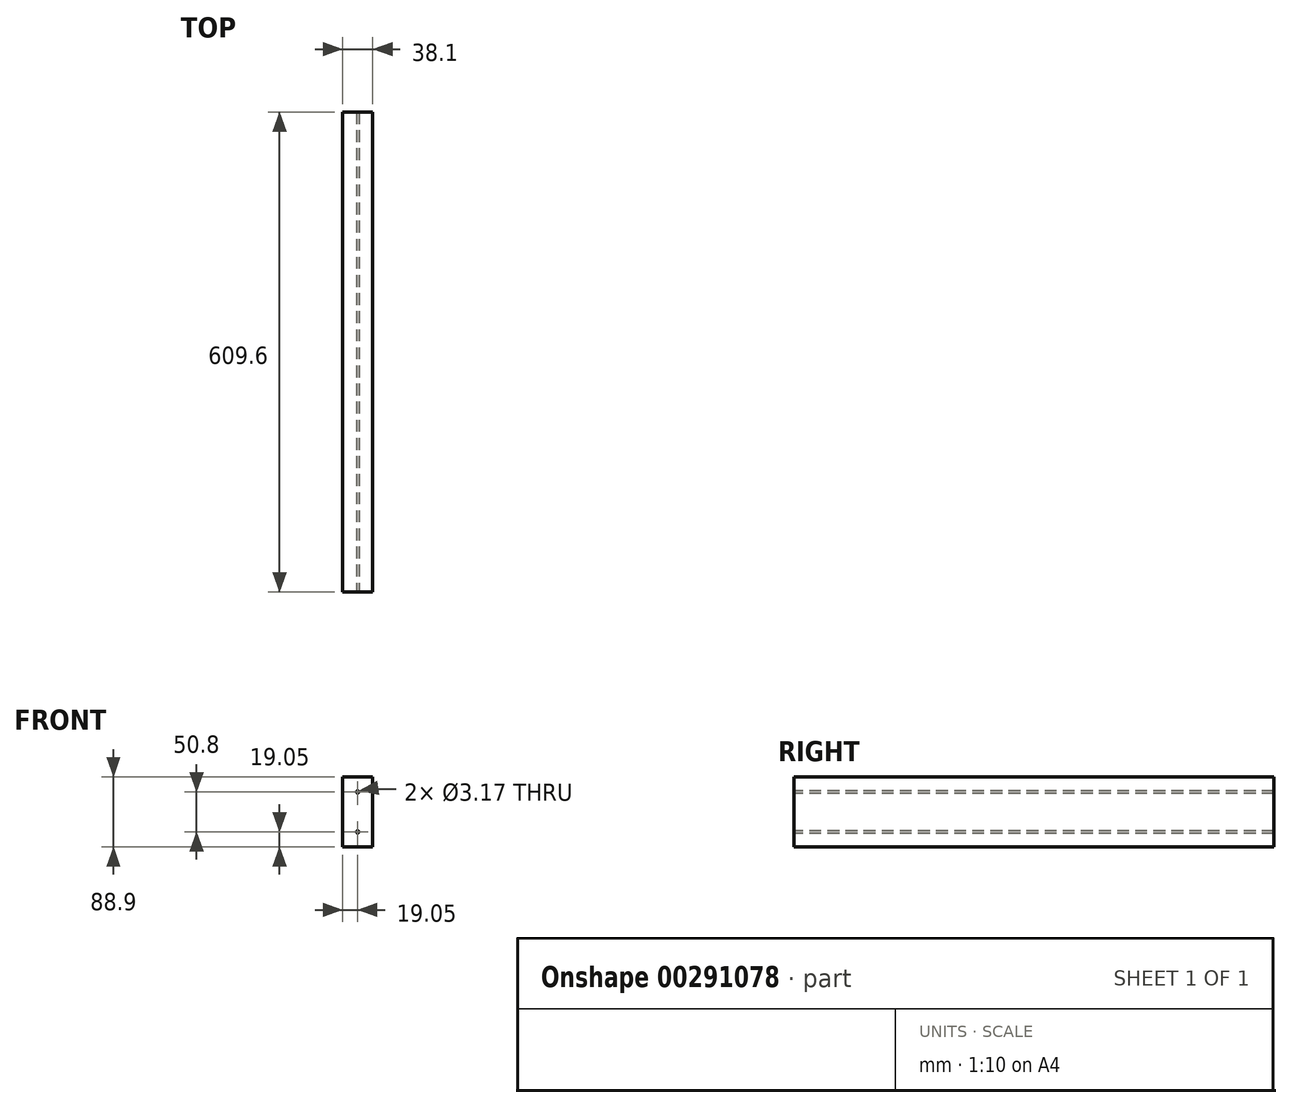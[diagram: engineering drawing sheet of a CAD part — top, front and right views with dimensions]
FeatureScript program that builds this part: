
annotation { "Feature Type Name" : "Feature", "Feature Type Description" : "" }
export const myFeature = defineFeature(function(context is Context, id is Id, definition is map)
    precondition{}
    {
        {
            var Q0;
            Q0=qCreatedBy(makeId("Right.planeOp"),FACE);
            var sketch = newSketch(context, id + "F0", { "sketchPlane" : qUnion([Q0])});
            skLineSegment(sketch, "E0.bottom", {"start": v(0, 0) * mm, "end": v(609.6, 0) * mm});
            skLineSegment(sketch, "E0.top", {"start": v(0, -88.9) * mm, "end": v(609.6, -88.9) * mm});
            skLineSegment(sketch, "E0.left", {"start": v(0, 0) * mm, "end": v(0, -88.9) * mm});
            skLineSegment(sketch, "E0.right", {"start": v(609.6, 0) * mm, "end": v(609.6, -88.9) * mm});
            skSolve(sketch);
        }
        {
            var Q0;
            Q0 = qSketchRegion(id + "F0", true);
            extrude(context, id + "F1", {"entities" : qUnion([Q0]), "oppositeDirection" : true, "depth" : 38.1 * mm});
        }
        {
            var Q0;
            Q0=qCreatedBy(makeId("Front.planeOp"),FACE);
            var sketch = newSketch(context, id + "F2", { "sketchPlane" : qUnion([Q0])});
            skCircle(sketch, "E1", {"center": v(-19.05, -19.05) * mm, "radius": 1.59 * mm});
            skCircle(sketch, "E2.0.1.0", {"center": v(-19.05, -69.85) * mm, "radius": 1.59 * mm});
            skLineSegment(sketch, "E2.direction1", {"start": v(-19.05, -19.05) * mm, "end": v(6.35, -19.05) * mm, "construction": true});
            skLineSegment(sketch, "E2.direction2", {"start": v(-19.05, -19.05) * mm, "end": v(-19.05, -69.85) * mm, "construction": true});
            skSolve(sketch);
        }
        {
            var Q0;
            Q0 = qSketchRegion(id + "F2", true);
            extrude(context, id + "F3", {"entities" : qUnion([Q0]), "operationType" : NewBodyOperationType.REMOVE, "endBound" : BoundingType.THROUGH_ALL, "oppositeDirection" : true, "depth" : 25.4 * mm});
        }
    });
